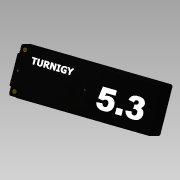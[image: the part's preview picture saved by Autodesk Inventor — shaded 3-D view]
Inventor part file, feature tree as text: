
AUTODESK INVENTOR PART (.ipt)
format: ipt  version: 2015 SP1 (Build 190203100, 203)  size: 205,312 bytes
history: native  units: mm
features: extrude x4, fillet x4, sketch x2
ambient origin geometry x8: Origin, YZ Plane, XZ Plane, XY Plane, X Axis, Y Axis, Z Axis, Center Point
bodies: Solid1 (feature_tree)
feature tree (10):
  sketch  "Sketch1"  dims[d0=138.42mm d1=46.73mm]
  extrude  "Extrusion1"  Depth=46.73mm
  extrude  "Extrusion2"  Depth=0.25mm
  extrude  "Extrusion3"  Depth=0.25mm
  extrude  "Extrusion4"  Depth=0.25mm
  fillet  "Fillet1"  Radius=4.525mm
  fillet  "Fillet2"  Radius=4.525mm
  fillet  "Fillet3"  Radius=8.365mm
  fillet  "Fillet4"  Radius=8.365mm
  sketch  "Sketch3"  dims[d2=4.0mm d3=4.0mm d5=4.525mm d7=4.525mm d11=4.525mm d13=4.525mm d14=8.365mm d15=8.365mm d16=2.0mm d17=2.0mm d18=25.3mm d19=0.0mm d20=20.2mm d21=0.0mm d22=6.0mm d23=0.0mm d24=11.1mm d25=0.0mm d26=2.0mm d27=1.0mm d28=0.25mm d29=0.25mm d34=18.84mm]
